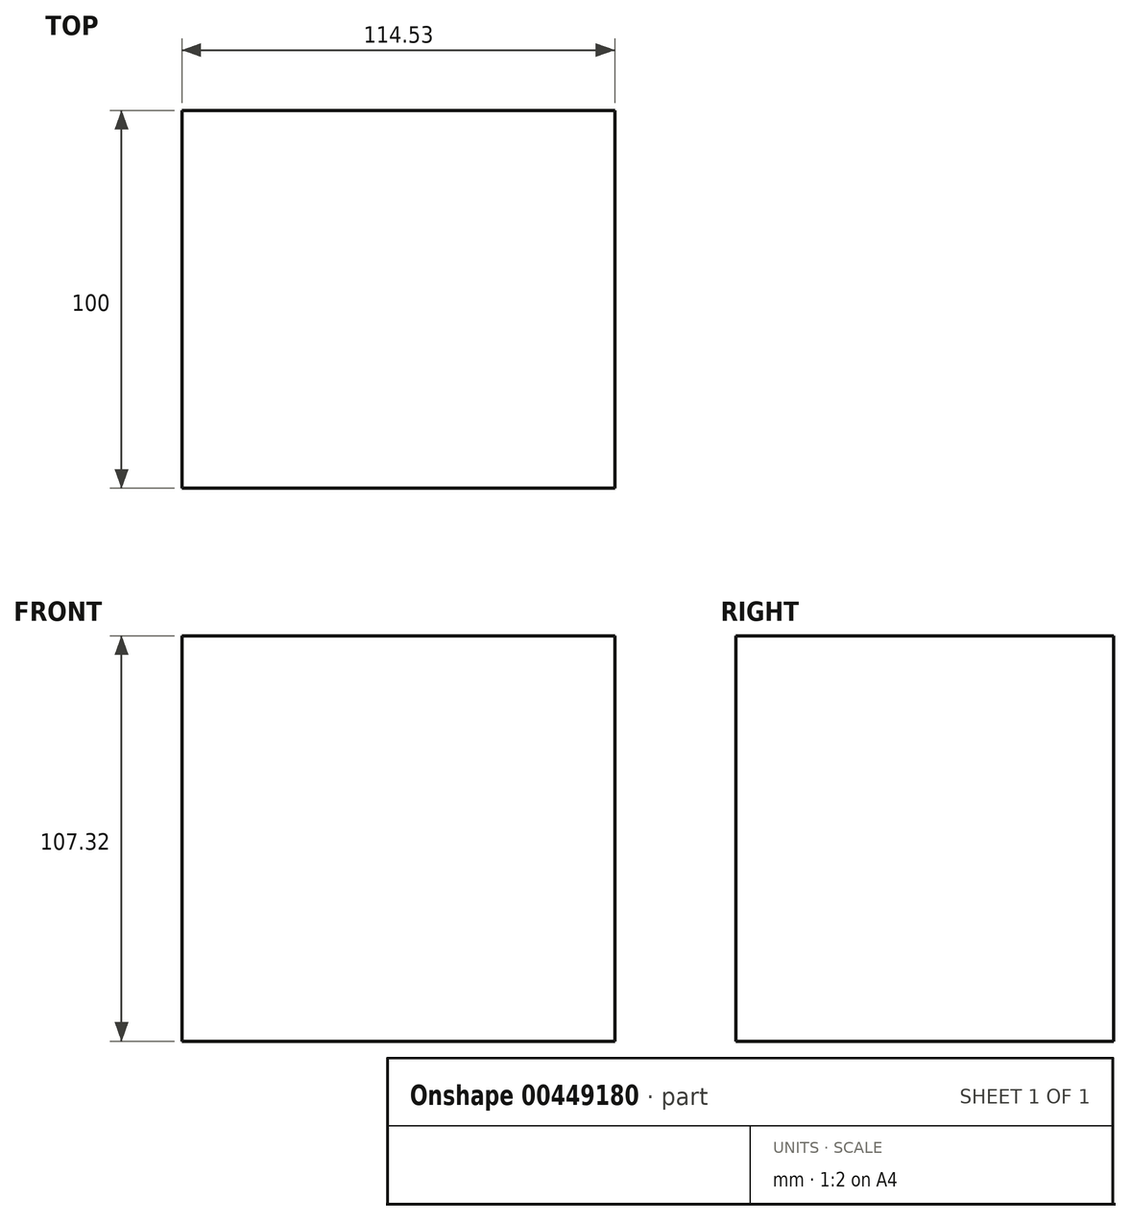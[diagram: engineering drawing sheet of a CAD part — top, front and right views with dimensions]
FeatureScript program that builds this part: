
annotation { "Feature Type Name" : "Feature", "Feature Type Description" : "" }
export const myFeature = defineFeature(function(context is Context, id is Id, definition is map)
    precondition{}
    {
        {
            var Q0;
            Q0=qCreatedBy(makeId("Front.planeOp"),FACE);
            var sketch = newSketch(context, id + "F0", { "sketchPlane" : qUnion([Q0])});
            skLineSegment(sketch, "E0.bottom", {"start": v(-56.7, 53.89) * mm, "end": v(57.83, 53.89) * mm});
            skLineSegment(sketch, "E0.top", {"start": v(-56.7, -53.43) * mm, "end": v(57.83, -53.43) * mm});
            skLineSegment(sketch, "E0.left", {"start": v(-56.7, 53.89) * mm, "end": v(-56.7, -53.43) * mm});
            skLineSegment(sketch, "E0.right", {"start": v(57.83, 53.89) * mm, "end": v(57.83, -53.43) * mm});
            skSolve(sketch);
        }
        {
            var Q0;
            Q0 = qSketchRegion(id + "F0", true);
            extrude(context, id + "F1", {"entities" : qUnion([Q0]), "domain" : OperationDomain.MODEL, "flatOperationType" : FlatOperationType.REMOVE, "depth" : 50 * mm, "offsetDistance" : 25 * mm, "hasSecondDirection" : true, "secondDirectionOppositeDirection" : true, "secondDirectionDepth" : 50 * mm});
        }
    });
